# Revit family: 342320xx1--Vitreous china close-coupled WC with horizontal outlet-Dama Retro-342320xx1
name_source: partatom
category: Plumbing Fixtures
units: mm (PartAtom-declared; Revit-internal decimal feet)

## family parameters
Always vertical = Yes
Cut with Voids When Loaded = No
OmniClass Number = 23.45.05.21.11
OmniClass Title = Water Closets
Part Type = Normal
Room Calculation Point = No
Round Connector Dimension = Use Diameter
Shared = No
Work Plane-Based = No

## types (2) — shared parameters
BIMobject category = WC
Description = Vitreous china close-coupled WC with horizontal outlet
Drain Diameter = 102 mm
Edition number = 1
Fixing kit = Included
Flushing system = Washdown
Height = 745 mm  [stored 2.44423 ft]
IFC Classification = Sanitary Terminal
Installation type = Floorstanding
Length = 405 mm  [stored 1.32874 ft]
Manufacturer URL = http://www.roca.com
Manufacturer name = Roca
Model = 342320..1
NBS Reference Code = 35-65-90-97
NBS Reference Description = Wc Systems
Nominal height = 74500
Nominal width = 68500
Outlet Type = Horizontal
Product Guid = 647a3817-e952-430f-a87b-5be83a3328a8
Product data url = http://bimobject.com
Product family = Dama Retro
Product group = TOILETS
QR code = https://www.roca.com
Shape = Round
URL = http://www.export.roca.com
Uniclass 1.4 Code = L7216
Uniclass 1.4 Description = Toilets
Uniclass 2.0 Code = SS-35-65-90-97
Uniclass 2.0 Description = Wc Systems
Water Inlet Diameter = 55 mm  [stored 0.180446 ft]
Width = 685 mm
zero-valued in all types: Weight Net (Kg)

## per-type parameters (varying)
| type | Imported Category Visibility 01 | Imported Category Visibility 02 | Primary Material | Product SKU |
| 342320001 White | Yes | No | White-Dama Retro-Roca | 342320001 |
| 342320171 Pergamon | No | Yes | Pergamon-Dama Retro-Roca | 342320171 |

note: [stored X ft] marks values corroborated as IEEE doubles in the binary element streams (Revit-internal decimal feet)

## geometry (parser evidence)
native form markers: Blend x4, Sweep x13
no freeform markers — native parametric forms only
